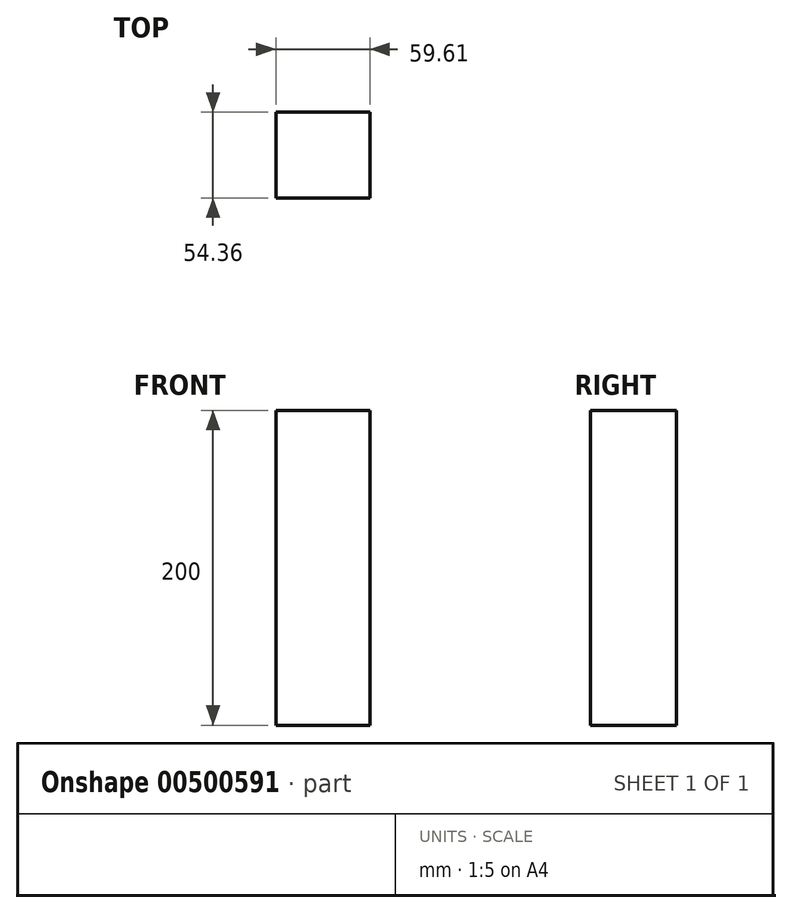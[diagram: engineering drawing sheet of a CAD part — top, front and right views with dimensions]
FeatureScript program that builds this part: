
annotation { "Feature Type Name" : "Feature", "Feature Type Description" : "" }
export const myFeature = defineFeature(function(context is Context, id is Id, definition is map)
    precondition{}
    {
        {
            var Q0;
            Q0=qCreatedBy(makeId("Top.planeOp"),FACE);
            var sketch = newSketch(context, id + "F0", { "sketchPlane" : qUnion([Q0])});
            skLineSegment(sketch, "E0.bottom", {"start": v(0, 0) * mm, "end": v(-59.6, 0) * mm});
            skLineSegment(sketch, "E0.top", {"start": v(0, 54.36) * mm, "end": v(-59.6, 54.36) * mm});
            skLineSegment(sketch, "E0.left", {"start": v(0, 0) * mm, "end": v(0, 54.36) * mm});
            skLineSegment(sketch, "E0.right", {"start": v(-59.6, 0) * mm, "end": v(-59.6, 54.36) * mm});
            skSolve(sketch);
        }
        {
            var Q0;
            Q0=makeQuery(id+"F0.imprint","IMPRINT",FACE,{"disambiguationData":[TD([[makeQuery(id+"F0.imprint","IMPRINT",EDGE,{"derivedFrom":sQuery(id+"F0.wireOp",EDGE,"E0.bottom")}),-1.0]])]});
            extrude(context, id + "F1", {"entities" : qUnion([Q0]), "depth" : 200 * mm});
        }
    });
